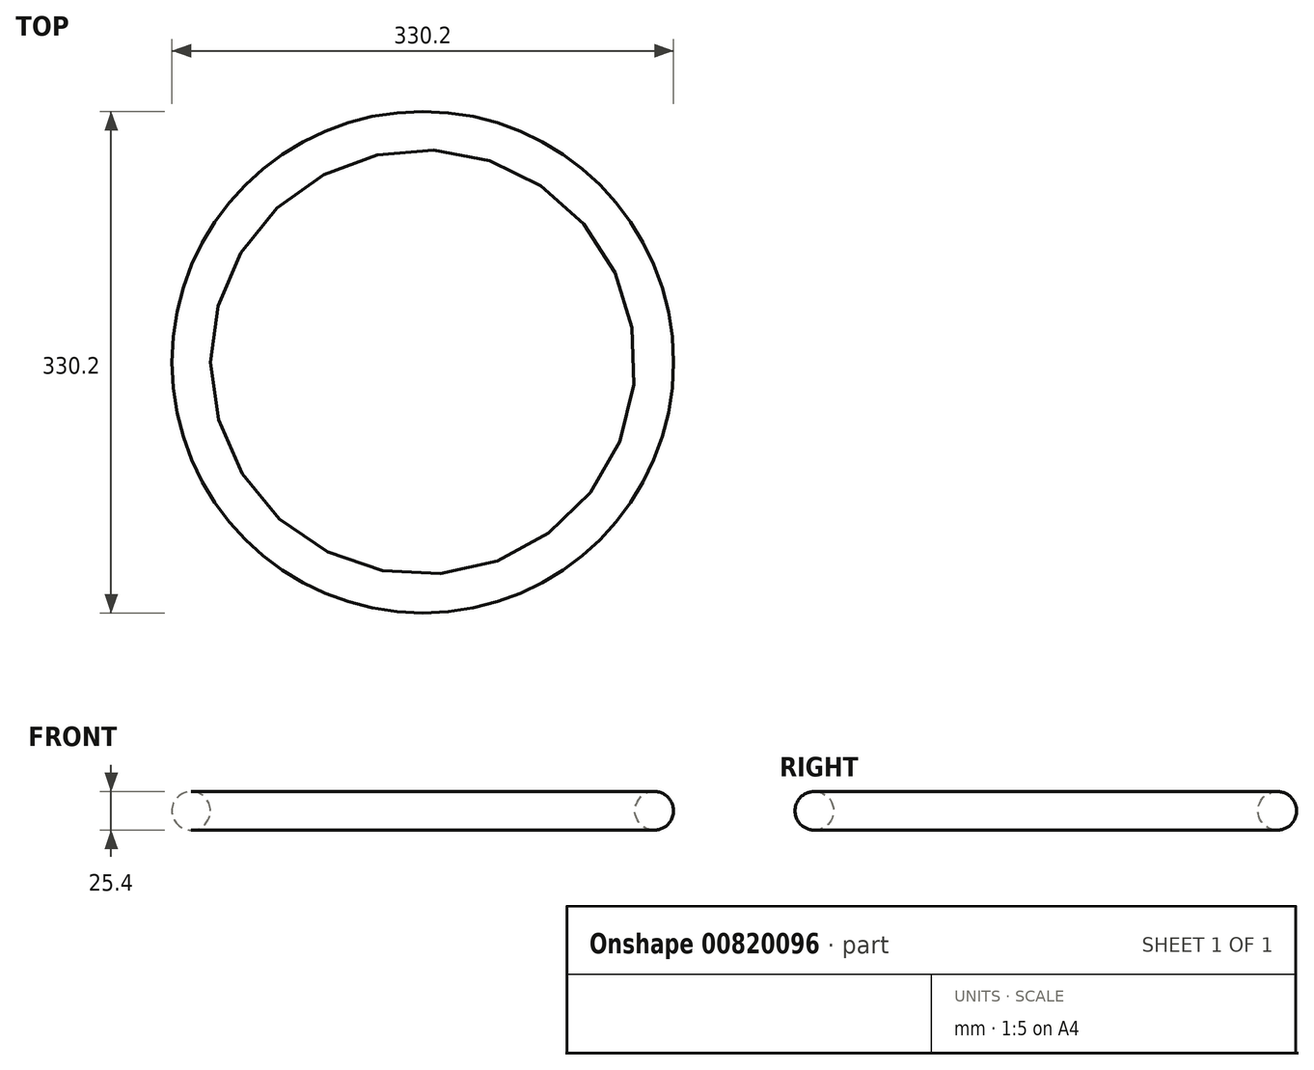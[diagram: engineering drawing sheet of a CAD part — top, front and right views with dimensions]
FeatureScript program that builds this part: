
annotation { "Feature Type Name" : "Feature", "Feature Type Description" : "" }
export const myFeature = defineFeature(function(context is Context, id is Id, definition is map)
    precondition{}
    {
        {
            var Q0;
            Q0=qCreatedBy(makeId("Front.planeOp"),FACE);
            var sketch = newSketch(context, id + "F0", { "sketchPlane" : qUnion([Q0])});
            skCircle(sketch, "E0", {"center": v(152.4, 0) * mm, "radius": 12.7 * mm});
            skLineSegment(sketch, "E1", {"start": v(0, -64.37) * mm, "end": v(0, 63.16) * mm, "construction": true});
            skSolve(sketch);
        }
        {
            var Q0;
            Q0=makeQuery(id+"F0.imprint","IMPRINT",FACE,{"disambiguationData":[TD([[makeQuery(id+"F0.imprint","IMPRINT",EDGE,{"derivedFrom":sQuery(id+"F0.wireOp",EDGE,"E0")}),1.0]])]});
            var Q1;
            Q1=sQuery(id+"F0.wireOp",EDGE,"E1");
            revolve(context, id + "F1", {"surfaceOperationType" : NewSurfaceOperationType.NEW, "entities" : qUnion([Q0]), "axis" : qUnion([Q1]), "revolveType" : RevolveType.FULL});
        }
    });
